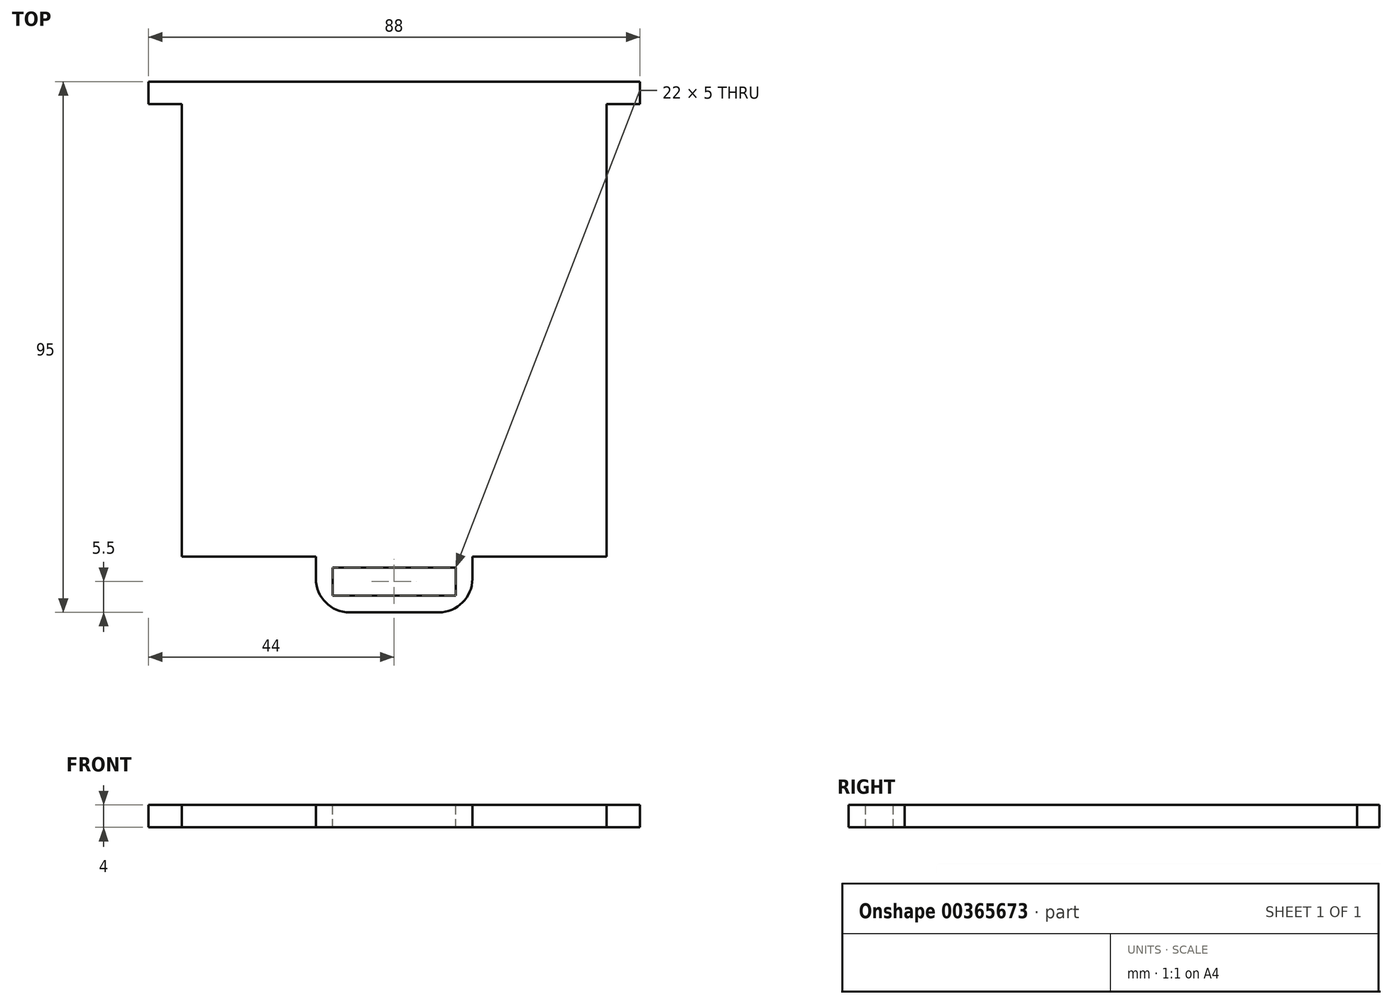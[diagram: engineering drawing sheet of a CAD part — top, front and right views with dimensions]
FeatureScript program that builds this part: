
annotation { "Feature Type Name" : "Feature", "Feature Type Description" : "" }
export const myFeature = defineFeature(function(context is Context, id is Id, definition is map)
    precondition{}
    {
        {
            var Q0;
            Q0=qCreatedBy(makeId("Top.planeOp"),FACE);
            var sketch = newSketch(context, id + "F0", { "sketchPlane" : qUnion([Q0])});
            skLineSegment(sketch, "E0.bottom", {"start": v(0, 0) * mm, "end": v(76, 0) * mm});
            skLineSegment(sketch, "E0.top", {"start": v(0, 85) * mm, "end": v(76, 85) * mm});
            skLineSegment(sketch, "E0.left", {"start": v(0, 0) * mm, "end": v(0, 85) * mm});
            skLineSegment(sketch, "E0.right", {"start": v(76, 0) * mm, "end": v(76, 85) * mm});
            skLineSegment(sketch, "E1", {"start": v(38, 0) * mm, "end": v(38, -10) * mm, "construction": true});
            skLineSegment(sketch, "E2.bottom", {"start": v(24, 0) * mm, "end": v(52, 0) * mm});
            skLineSegment(sketch, "E2.top", {"start": v(30, -10) * mm, "end": v(46, -10) * mm});
            skLineSegment(sketch, "E2.left", {"start": v(24, 0) * mm, "end": v(24, -4) * mm});
            skLineSegment(sketch, "E2.right", {"start": v(52, 0) * mm, "end": v(52, -4) * mm});
            skPoint(sketch, "E3", {"position": v(38, -10) * mm});
            skPoint(sketch, "E4.visualSharp", {"position": v(24, -10) * mm});
            skArc(sketch, "E4.filletArc", {"start": v(24, -4) * mm, "mid": v(25.76, -8.24) * mm, "end": v(30, -10) * mm});
            skPoint(sketch, "E5.visualSharp", {"position": v(52, -10) * mm});
            skArc(sketch, "E5.filletArc", {"start": v(46, -10) * mm, "mid": v(50.24, -8.24) * mm, "end": v(52, -4) * mm});
            skLineSegment(sketch, "E6.bottom", {"start": v(76, 85) * mm, "end": v(82, 85) * mm});
            skLineSegment(sketch, "E6.top", {"start": v(76, 81) * mm, "end": v(82, 81) * mm});
            skLineSegment(sketch, "E6.left", {"start": v(76, 85) * mm, "end": v(76, 81) * mm});
            skLineSegment(sketch, "E6.right", {"start": v(82, 85) * mm, "end": v(82, 81) * mm});
            skLineSegment(sketch, "E7.bottom", {"start": v(0, 85) * mm, "end": v(-6, 85) * mm});
            skLineSegment(sketch, "E7.top", {"start": v(0, 81) * mm, "end": v(-6, 81) * mm});
            skLineSegment(sketch, "E7.left", {"start": v(0, 85) * mm, "end": v(0, 81) * mm});
            skLineSegment(sketch, "E7.right", {"start": v(-6, 85) * mm, "end": v(-6, 81) * mm});
            skSolve(sketch);
        }
        {
            var Q0;
            Q0 = qSketchRegion(id + "F0", true);
            extrude(context, id + "F1", {"entities" : qUnion([Q0]), "depth" : 4 * mm});
        }
        {
            var Q0;
            Q0=makeQuery(id+"F1.opExtrude","CAP_FACE",FACE,{"disambiguationData":[OSD([sQuery(id+"F0.wireOp",EDGE,"E0.bottom"),sQuery(id+"F0.wireOp",EDGE,"E0.top"),sQuery(id+"F0.wireOp",EDGE,"E0.left"),sQuery(id+"F0.wireOp",EDGE,"E0.right"),sQuery(id+"F0.wireOp",EDGE,"E2.top"),sQuery(id+"F0.wireOp",EDGE,"E2.left"),sQuery(id+"F0.wireOp",EDGE,"E2.right"),sQuery(id+"F0.wireOp",EDGE,"E4.filletArc"),sQuery(id+"F0.wireOp",EDGE,"E5.filletArc")])],"isStart":false});
            var sketch = newSketch(context, id + "F2", { "sketchPlane" : qUnion([Q0])});
            skLineSegment(sketch, "E8.bottom", {"start": v(27, -2) * mm, "end": v(49, -2) * mm});
            skLineSegment(sketch, "E8.top", {"start": v(27, -7) * mm, "end": v(49, -7) * mm});
            skLineSegment(sketch, "E8.left", {"start": v(27, -2) * mm, "end": v(27, -7) * mm});
            skLineSegment(sketch, "E8.right", {"start": v(49, -2) * mm, "end": v(49, -7) * mm});
            skLineSegment(sketch, "E9", {"start": v(24, 0) * mm, "end": v(52, 0) * mm, "construction": true});
            skPoint(sketch, "E10", {"position": v(38, -2) * mm});
            skPoint(sketch, "E11", {"position": v(38, 0) * mm});
            skLineSegment(sketch, "E12", {"start": v(38, 0) * mm, "end": v(38, -2) * mm, "construction": true});
            skSolve(sketch);
        }
        {
            var Q0;
            Q0 = qSketchRegion(id + "F2", true);
            extrude(context, id + "F3", {"entities" : qUnion([Q0]), "operationType" : NewBodyOperationType.REMOVE, "endBound" : BoundingType.THROUGH_ALL, "oppositeDirection" : true, "depth" : 25 * mm});
        }
    });
